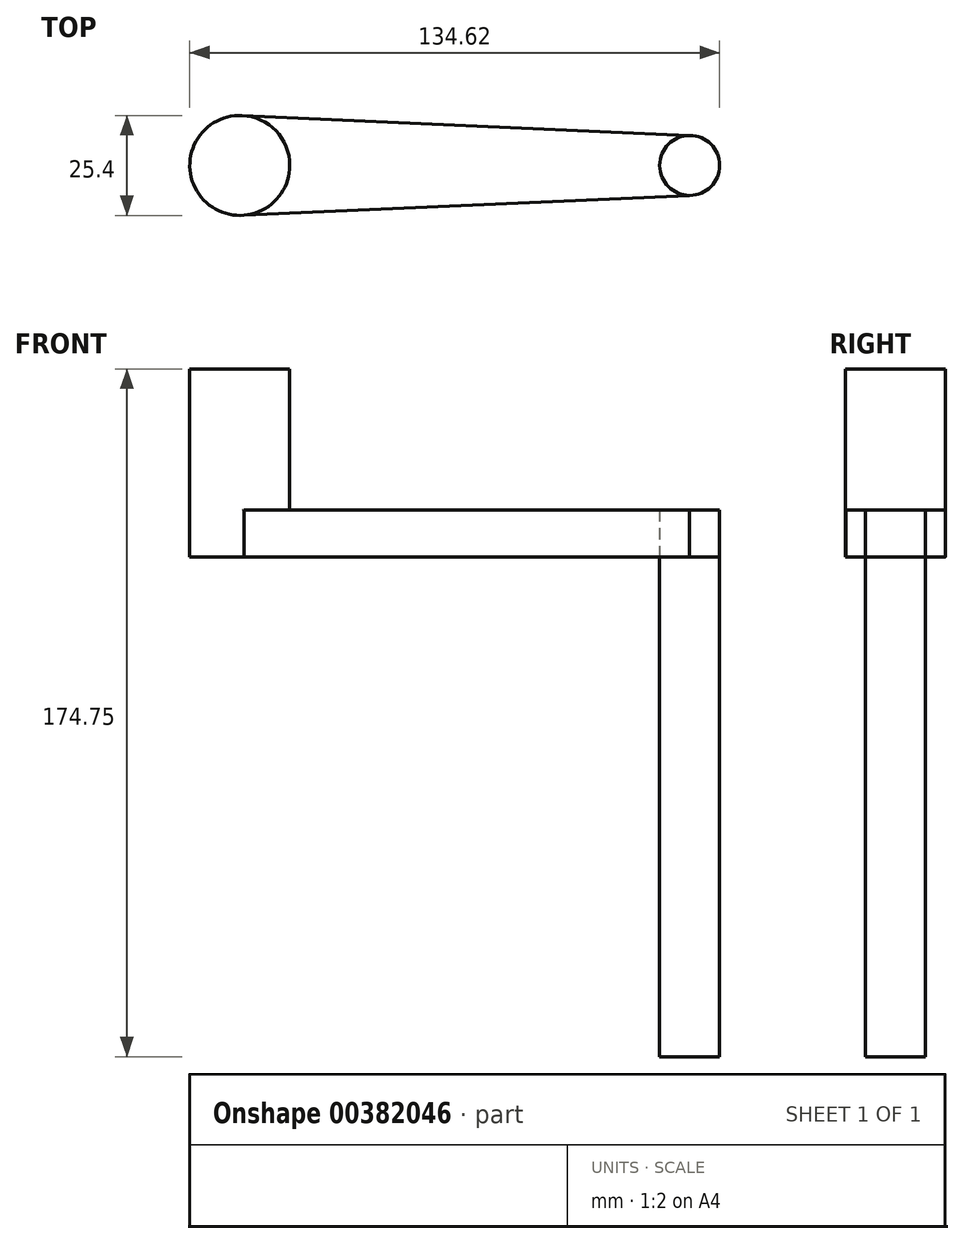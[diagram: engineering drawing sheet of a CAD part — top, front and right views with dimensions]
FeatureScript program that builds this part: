
annotation { "Feature Type Name" : "Feature", "Feature Type Description" : "" }
export const myFeature = defineFeature(function(context is Context, id is Id, definition is map)
    precondition{}
    {
        {
            var Q0;
            Q0=qCreatedBy(makeId("Top.planeOp"),FACE);
            var sketch = newSketch(context, id + "F0", { "sketchPlane" : qUnion([Q0])});
            skCircle(sketch, "E0", {"center": v(0, 0) * mm, "radius": 12.7 * mm});
            skSolve(sketch);
        }
        {
            var Q0;
            Q0=makeQuery(id+"F0.imprint","IMPRINT",FACE,{"disambiguationData":[TD([[makeQuery(id+"F0.imprint","IMPRINT",EDGE,{"derivedFrom":sQuery(id+"F0.wireOp",EDGE,"E0")}),1.0]])]});
            extrude(context, id + "F1", {"entities" : qUnion([Q0]), "depth" : 47.75 * mm});
        }
        {
            var Q0;
            Q0=qCreatedBy(makeId("Top.planeOp"),FACE);
            var sketch = newSketch(context, id + "F2", { "sketchPlane" : qUnion([Q0])});
            skCircle(sketch, "E1.0", {"center": v(0, 0) * mm, "radius": 12.7 * mm});
            skCircle(sketch, "E2", {"center": v(114.3, 0) * mm, "radius": 7.62 * mm});
            skLineSegment(sketch, "E3", {"start": v(0, -12.7) * mm, "end": v(114.3, -7.62) * mm});
            skLineSegment(sketch, "E4", {"start": v(114.3, 7.62) * mm, "end": v(0, 12.71) * mm});
            skSolve(sketch);
        }
        {
            var Q0;
            {var subQ0=sQuery(id+"F2.wireOp",EDGE,"E4");var subQ1=sQuery(id+"F2.wireOp",EDGE,"E1.0");var subQ2=makeQuery(id+"F2.imprint","INTERSECT",VERTEX,{"derivedFrom":[subQ1,subQ0]});Q0=makeQuery(id+"F2.imprint","IMPRINT",FACE,{"disambiguationData":[TD([[makeQuery(id+"F2.imprint","IMPRINT",EDGE,{"disambiguationData":[TD([[subQ2,1.0]])],"derivedFrom":subQ1}),-1.0]])]});}
            extrude(context, id + "F3", {"entities" : qUnion([Q0]), "operationType" : NewBodyOperationType.ADD, "depth" : 11.94 * mm});
        }
        {
            var Q0;
            {var subQ0=sQuery(id+"F2.wireOp",EDGE,"E2");var subQ1=makeQuery(id+"F2.imprint","INTERSECT",VERTEX,{"derivedFrom":[subQ0,sQuery(id+"F2.wireOp",EDGE,"E3")]});Q0=makeQuery(id+"F2.imprint","IMPRINT",FACE,{"disambiguationData":[TD([[makeQuery(id+"F2.imprint","IMPRINT",EDGE,{"disambiguationData":[TD([[subQ1,1.0]])],"derivedFrom":subQ0}),1.0]])]});}
            extrude(context, id + "F4", {"entities" : qUnion([Q0]), "operationType" : NewBodyOperationType.ADD, "oppositeDirection" : true, "depth" : 127 * mm});
        }
        {
            var Q0;
            {var subQ0=sQuery(id+"F2.wireOp",EDGE,"E2");var subQ1=makeQuery(id+"F2.imprint","INTERSECT",VERTEX,{"derivedFrom":[subQ0,sQuery(id+"F2.wireOp",EDGE,"E3")]});Q0=makeQuery(id+"F2.imprint","IMPRINT",FACE,{"disambiguationData":[TD([[makeQuery(id+"F2.imprint","IMPRINT",EDGE,{"disambiguationData":[TD([[subQ1,1.0]])],"derivedFrom":subQ0}),1.0]])]});}
            extrude(context, id + "F5", {"entities" : qUnion([Q0]), "operationType" : NewBodyOperationType.REMOVE, "depth" : 11.94 * mm});
        }
        {
            var Q0;
            {var subQ0=sQuery(id+"F2.wireOp",EDGE,"E2");var subQ1=makeQuery(id+"F2.imprint","INTERSECT",VERTEX,{"derivedFrom":[subQ0,sQuery(id+"F2.wireOp",EDGE,"E3")]});Q0=makeQuery(id+"F2.imprint","IMPRINT",FACE,{"disambiguationData":[TD([[makeQuery(id+"F2.imprint","IMPRINT",EDGE,{"disambiguationData":[TD([[subQ1,1.0]])],"derivedFrom":subQ0}),1.0]])]});}
            extrude(context, id + "F6", {"entities" : qUnion([Q0]), "depth" : 11.94 * mm});
        }
    });
